# Revit family: IS_ConnectAir_E0299_BIM_DE
name_source: partatom
category: Plumbing Fixtures
revit_build: Autodesk Revit MEP 2014 (Build: 20130308_1515(x64)
units: mm (PartAtom-declared; Revit-internal decimal feet)

## types (4) — shared parameters
Accessories = www.idealstandard.de\ersatzteile
AreaUnits = millimeters
Assembly Code = C1030200
AssetType = Fixed
Brand = Ideal Standard
CodePerformance = DIN EN 14688 CL 25, DIN EN 31
ConnectionType = Plumbing
DrainSize = 42 mm  [stored 0.137795 ft]
DurationUnit = year
ExpectedLife = 25
Features = Connect Air 55cm washbasin, 1 taphole with overflow
GrossWeight = 0
IfcExportAs = IfcSanitaryType
IfcExportType = WASHHANDBASIN
InstallationInstructions = www.idealstandard.de\produkte
LinearUnits = millimeters
ManufacturerURL = www.idealstandard.de
Material = Vitreous china
NBSDescription = Pedestal wash basins
NBSReference = 45-35-70/365
NettWeight = 13,94 kg
NominalHeight = 160 mm
NominalLength = 461 mm
NominalWidth = 551 mm
ProductInformation = www.idealstandard.de\produkte
Shape = Sculptured
Size = 550x460x160mm
Space = Internal
URL = www.idealstandard.com
Uniclass2015Code = Pr_40_20_96_63
Uniclass2015Title = Pedestal wash basins
Uniclass2015Version = Products v1.1
Version = 1
VolumeUnits = Litres
WarrantyDescription = Manufacturers Warranty
WarrantyDurationUnit = year
WashHandBasinMounting = i.e.Wall Hung
WashHandBasinType = Hand Rinse
zero-valued in all types: CWFU, Cost, HWFU, WFU

## per-type parameters (varying)
| type | BIMObjectName | BarCode | Color | Default Elevation | Description | E0309 | E0339 | Finish | Model | ModelNumber | ModelReference | Name |
| E029901 - Connect Air 55cm washbasin, 1 taphole with overflow(E0309) | ISI_IdealStandard_PedestalWashBasins_ConnectAir_E029901 | 5017830514442 | white | 850 mm  [stored 2.78871 ft] | E029901 Connect Air 55cm washbasin, 1 taphole with overflow | Yes | No | white | E029901 | E029901 | E029901 Connect Air 55cm washbasin, 1 taphole with overflow | PedestalWashBasins_ConnectAir_E029901_IdealStandard |
| E0299MA - Connect Air 55cm washbasin, 1 taphole with overflow(E0309) | ISI_IdealStandard_PedestalWashBasins_ConnectAir_E0299MA | 5017830518419 | white with ideal plus | 850 mm  [stored 2.78871 ft] | E0299MA Connect Air 55cm washbasin, 1 taphole with overflow | Yes | No | white with ideal plus | E0299MA | E0299MA | E0299MA Connect Air 55cm washbasin, 1 taphole with overflow | PedestalWashBasins_ConnectAir_E0299MA_IdealStandard |
| E029901 - Connect Air 55cm washbasin, 1 taphole with overflow(E0339) | ISI_IdealStandard_PedestalWashBasins_ConnectAir_E029901 | 5017830514442 | white | 840 mm  [stored 2.75591 ft] | E029901 Connect Air 55cm washbasin, 1 taphole with overflow | No | Yes | white | E029901 | E029901 | E029901 Connect Air 55cm washbasin, 1 taphole with overflow | PedestalWashBasins_ConnectAir_E029901_IdealStandard |
| E0299MA - Connect Air 55cm washbasin, 1 taphole with overflow(E0339) | ISI_IdealStandard_PedestalWashBasins_ConnectAir_E0299MA | 5017830518419 | white with ideal plus | 840 mm  [stored 2.75591 ft] | E0299MA Connect Air 55cm washbasin, 1 taphole with overflow | No | Yes | white with ideal plus | E0299MA | E0299MA | E0299MA Connect Air 55cm washbasin, 1 taphole with overflow | PedestalWashBasins_ConnectAir_E0299MA_IdealStandard |

note: [stored X ft] marks values corroborated as IEEE doubles in the binary element streams (Revit-internal decimal feet)

## geometry (parser evidence)
native form markers: Sweep x8
no freeform markers — native parametric forms only
